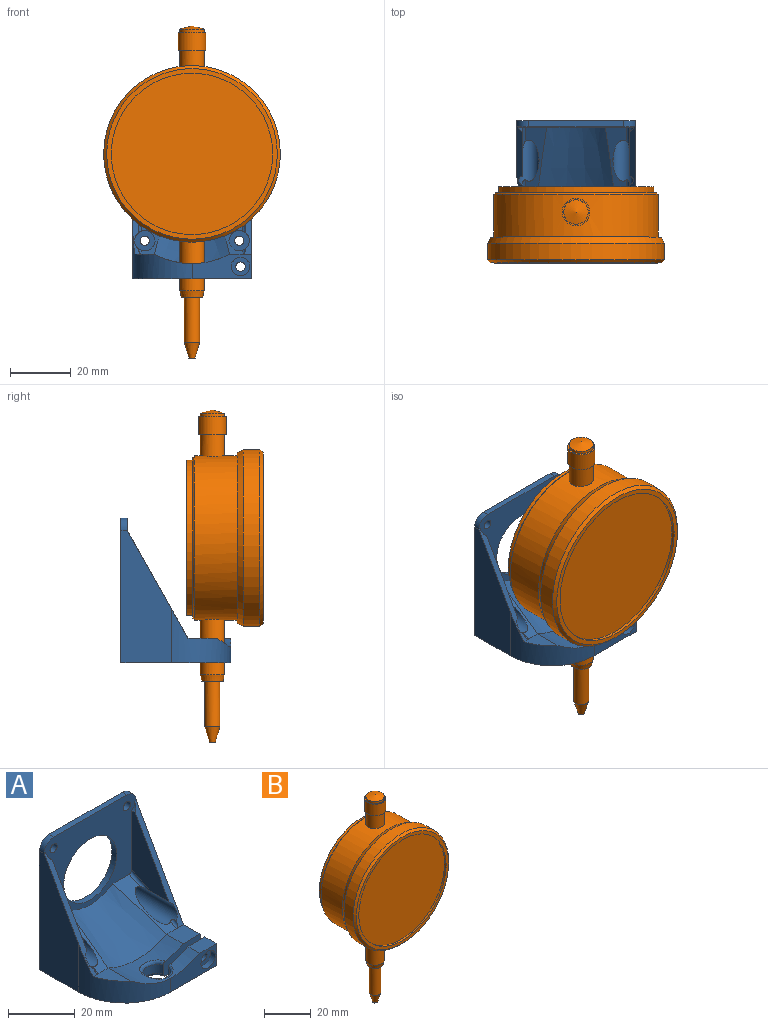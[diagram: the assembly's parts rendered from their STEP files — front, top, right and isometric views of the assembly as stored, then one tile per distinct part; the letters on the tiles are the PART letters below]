
ASSEMBLY  parts=2 mates=3
PART A: 55 faces, bbox 39.5x36.8x48 mm
  f0: plane 25.59x15.94mm, normal (-1,0,0), area 208.1mm2, adj f17,f35,f45,f48,f52
  f1: plane 25.59x15.94mm, normal (1,0,0), area 208.1mm2, adj f17,f36,f43,f47,f50
  f2: cylinder r=1.53mm len=3.06mm, axis (0,1,0), area 19.2mm2, adj f6,f46
  f3: plane 0.47x0.24mm, normal (-1,0,0), area 0mm2, adj f35,f45,f49
  f4: cylinder r=1.53mm len=3.06mm, axis (0,1,0), area 19.2mm2, adj f6,f44
  f5: plane 0.47x0.24mm, normal (1,0,0), area 0mm2, adj f36,f43,f51
  f6: plane 47.5x39mm, normal (0,1,0), area 1390.4mm2, adj f2,f4,f7,f11,f14,f15,f16,f18
  f7: plane 39x36mm, normal (0,0,-1), area 1212.4mm2, adj f6,f9,f10,f11,f13,f16,f22,f37
  f8: cylinder r=27mm len=24.74mm, axis (0,1,0), area 236.9mm2, adj f9,f10,f12,f20,f21,f22,f37,f41
  f9: plane 15.62x8.07mm, normal (0,1,0), area 103.1mm2, adj f7,f8,f13,f20,f23,f25,f53,f54
  f10: plane 15.62x8.07mm, normal (0,-1,0), area 103.1mm2, adj f7,f8,f11,f12,f23,f24,f53,f54
  f11: plane 43.5x29mm, normal (1,0,0), area 658mm2, adj f6,f7,f10,f12,f35,f38
  f12: plane 7.13x7mm, normal (0,0,1), area 49.9mm2, adj f8,f10,f11,f35,f42
  f13: plane 8x5mm, normal (1,0,0), area 40mm2, adj f7,f9,f20,f22
  f14: plane 31x2mm, normal (0,0,1), area 62mm2, adj f6,f17,f38,f39
  f15: cylinder r=11.22mm len=22.44mm, axis (0,1,0), area 141mm2, adj f6,f17
  f16: plane 43.5x16.5mm, normal (-1,0,0), area 531.2mm2, adj f6,f7,f36,f37,f39
  f17: plane 39.21x32.71mm, normal (0,-1,0), area 675.4mm2, adj f0,f1,f14,f15,f18,f19,f35,f36
  f18: cylinder r=1.53mm len=3.06mm, axis (0,1,0), area 19.2mm2, adj f6,f17
  f19: cylinder r=1.53mm len=3.06mm, axis (0,1,0), area 19.2mm2, adj f6,f17
  f20: plane 7.13x5mm, normal (0,0,1), area 35.7mm2, adj f8,f9,f13,f22
  f21: plane 9.58x6.34mm, normal (0,0,1), area 37mm2, adj f8,f36,f37,f40
  f22: plane 19.5x8mm, normal (0,-1,0), area 101.6mm2, adj f7,f8,f13,f20,f27,f37
  f23: cylinder r=4.08mm len=8.16mm, axis (0,0,-1), area 81.2mm2, adj f9,f10,f53,f54
  f24: cylinder r=1.53mm len=21mm, axis (0,-1,0), area 201.9mm2, adj f10,f28
  f25: cylinder r=1.53mm len=3.06mm, axis (0,-1,0), area 28.8mm2, adj f9,f26
  f26: plane 6.12x6.12mm, normal (0,-1,0), area 22.1mm2, adj f25,f27
  f27: cylinder r=3.06mm len=6.12mm, axis (0,-1,0), area 38.5mm2, adj f22,f26
  f28: plane 6.83x5.92mm, normal (0,1,0), area 23mm2, adj f24,f29,f30,f31,f32,f33,f34
  f29: plane 8x3.42mm, normal (0,0,-1), area 27.3mm2, adj f6,f28,f30,f34
  f30: plane 8x2.96mm, normal (-0.87,0,-0.5), area 27.3mm2, adj f6,f28,f29,f31
  f31: plane 8x2.96mm, normal (-0.87,0,0.5), area 27.3mm2, adj f6,f28,f30,f32
  f32: plane 8x3.42mm, normal (0,0,1), area 27.3mm2, adj f6,f28,f31,f33
  f33: plane 8x2.96mm, normal (0.87,0,0.5), area 27.3mm2, adj f6,f28,f32,f34
  f34: plane 8x2.96mm, normal (0.87,0,-0.5), area 27.3mm2, adj f6,f28,f29,f33
  f35: plane 35.69x20.19mm, normal (0,-0.87,0.49), area 73mm2, adj f0,f3,f11,f12,f17,f45,f48,f49
  f36: plane 35.69x20.19mm, normal (0,-0.87,0.49), area 70mm2, adj f1,f5,f16,f17,f21,f37,f43,f47
  f37: cylinder r=19.5mm len=19.5mm, axis (0,0,1), area 252.2mm2, adj f7,f8,f16,f21,f22,f36
  f38: cylinder r=4mm len=4mm, axis (0,-1,0), area 12.6mm2, adj f6,f11,f14,f17
  f39: cylinder r=4mm len=4mm, axis (0,1,0), area 12.6mm2, adj f6,f14,f16,f17
  f40: plane 20.49x10.49mm, normal (0,-0.45,0.89), area 67mm2, adj f17,f21,f41,f43,f50,f51
  f41: cone r=27mm half-angle=26.6deg, axis (0,-1,0), area 526.1mm2, adj f8,f17,f40,f42
  f42: plane 20.49x10.49mm, normal (0,-0.45,0.89), area 67mm2, adj f12,f17,f41,f45,f49,f52
  f43: cylinder r=3.37mm len=18.99mm, axis (0,1,0), area 274.5mm2, adj f1,f5,f36,f40,f44,f50,f51
  f44: plane 6.73x6.73mm, normal (0,-1,0), area 28.2mm2, adj f4,f43
  f45: cylinder r=3.37mm len=18.99mm, axis (0,1,0), area 274.5mm2, adj f0,f3,f35,f42,f46,f49,f52
  f46: plane 6.73x6.73mm, normal (0,-1,0), area 28.2mm2, adj f2,f45
  f47: cylinder r=3.37mm len=2.71mm, axis (0,1,0), area 2.4mm2, adj f1,f17,f36
  f48: cylinder r=3.37mm len=2.71mm, axis (0,1,0), area 2.4mm2, adj f0,f17,f35
  f49: cylinder r=1mm len=3.18mm, axis (0,-0.89,-0.45), area 3.6mm2, adj f3,f35,f42,f45
  f50: cylinder r=1mm len=8.27mm, axis (0,0.89,0.45), area 10.9mm2, adj f1,f17,f40,f43
  f51: cylinder r=1mm len=3.18mm, axis (0,0.89,0.45), area 3.6mm2, adj f5,f36,f40,f43
  f52: cylinder r=1mm len=8.27mm, axis (0,-0.89,-0.45), area 10.9mm2, adj f0,f17,f42,f45
  f53: bspline ~10.17x9.8mm, area 38.3mm2, adj f8,f9,f10,f23
  f54: torus R=5.08mm, axis (0,0,-1), area 40.8mm2, adj f7,f9,f10,f23
PART B: 24 faces, bbox 58x25x109 mm
  f0: cylinder r=25.5mm len=51mm, axis (0,1,0), area 320.4mm2, adj f1,f3
  f1: plane 51x51mm, normal (0,1,0), area 2042.8mm2, adj f0
  f2: cylinder r=27mm len=54mm, axis (0,1,0), area 2274.3mm2, adj f6,f8,f9,f20
  f3: plane 53x53mm, normal (0,1,0), area 163.4mm2, adj f0,f20
  f4: cylinder r=29mm len=58mm, axis (0,1,0), area 1002.2mm2, adj f21,f22
  f5: plane 56x56mm, normal (0,-1,0), area 256.8mm2, adj f16,f21
  f6: plane 56x56mm, normal (0,1,0), area 172.8mm2, adj f2,f22
  f7: plane 7x7mm, normal (0,0,-1), area 18.8mm2, adj f10,f19
  f8: cylinder r=4mm len=18.3mm, axis (0,0,1), area 456.1mm2, adj f2,f19
  f9: cylinder r=4mm len=8mm, axis (0,0,1), area 179.7mm2, adj f2,f14
  f10: cylinder r=2.5mm len=15mm, axis (0,0,1), area 235.6mm2, adj f7,f18
  f11: plane 2x2mm, normal (0,0,-1), area 3.1mm2, adj f18
  f12: cylinder r=4.5mm len=9mm, axis (0,0,-1), area 169.6mm2, adj f13,f14
  f13: plane 9x9mm, normal (0,0,1), area 13.4mm2, adj f12,f15
  f14: plane 9x9mm, normal (0,0,-1), area 13.4mm2, adj f9,f12
  f15: cylinder r=4mm len=8mm, axis (0,0,-1), area 25.1mm2, adj f13,f23
  f16: cylinder r=26.5mm len=53mm, axis (0,-1,0), area 166.5mm2, adj f5,f17
  f17: plane 53x53mm, normal (0,-1,0), area 2206.2mm2, adj f16
  f18: cone r=1mm half-angle=16.7deg, axis (0,0,1), area 57.4mm2, adj f10,f11
  f19: cone r=4mm half-angle=14deg, axis (0,0,1), area 48.6mm2, adj f7,f8
  f20: cone r=27mm half-angle=45deg, axis (0,-1,0), area 118.8mm2, adj f2,f3
  f21: cone r=28mm half-angle=45deg, axis (0,1,0), area 253.2mm2, adj f4,f5
  f22: cone r=29mm half-angle=26.6deg, axis (0,-1,0), area 400.4mm2, adj f4,f6
  f23: cone r=4mm half-angle=76deg, axis (0,0,-1), area 51.8mm2, adj f15
PLACE A at identity fixed
PLACE B t=(0,-21.64,13)mm
MATE parallel B.f0 <-> A.f17  axis (0,1,0) through (0,-21.64,13)mm
MATE slider B.f8 <-> A.f23  axis (0,0,1) through (0,-30,-32)mm
MATE planar A.f7 <-> B.f8  axis (0,0,-1) through (0.73,-15.99,-28)mm
